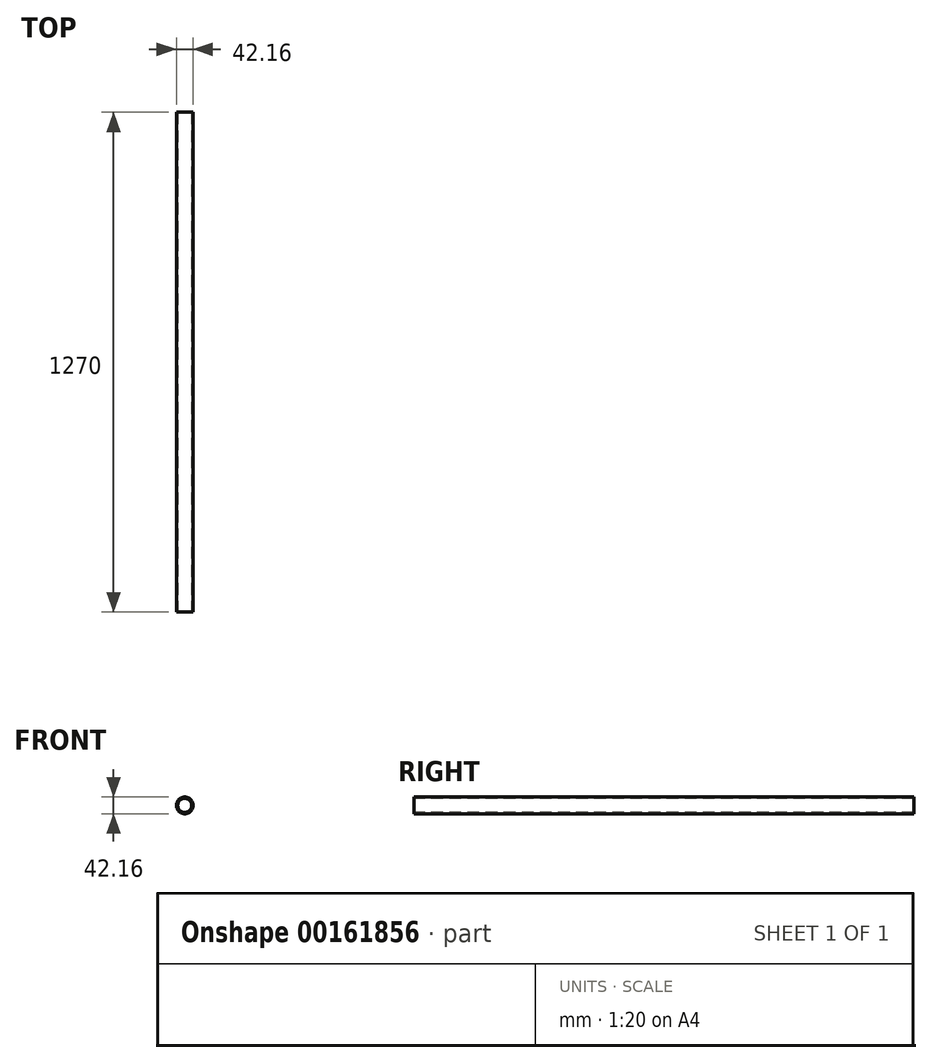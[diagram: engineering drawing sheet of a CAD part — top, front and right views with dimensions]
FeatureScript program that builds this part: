
annotation { "Feature Type Name" : "Feature", "Feature Type Description" : "" }
export const myFeature = defineFeature(function(context is Context, id is Id, definition is map)
    precondition{}
    {
        {
            var Q0;
            Q0=qCreatedBy(makeId("Front.planeOp"),FACE);
            var sketch = newSketch(context, id + "F0", { "sketchPlane" : qUnion([Q0])});
            skCircle(sketch, "E0", {"center": v(0, 0) * mm, "radius": 21.08 * mm});
            skCircle(sketch, "E1", {"center": v(0, 0) * mm, "radius": 17.78 * mm});
            skSolve(sketch);
        }
        {
            var Q0;
            Q0=sQuery(id+"F0.wireOp",EDGE,"E0");
            var Q1;
            Q1=sQuery(id+"F0.wireOp",EDGE,"E1");
            extrude(context, id + "F1", {"bodyType" : ToolBodyType.SURFACE, "surfaceEntities" : qUnion([Q0, Q1]), "depth" : 1270 * mm});
        }
    });
